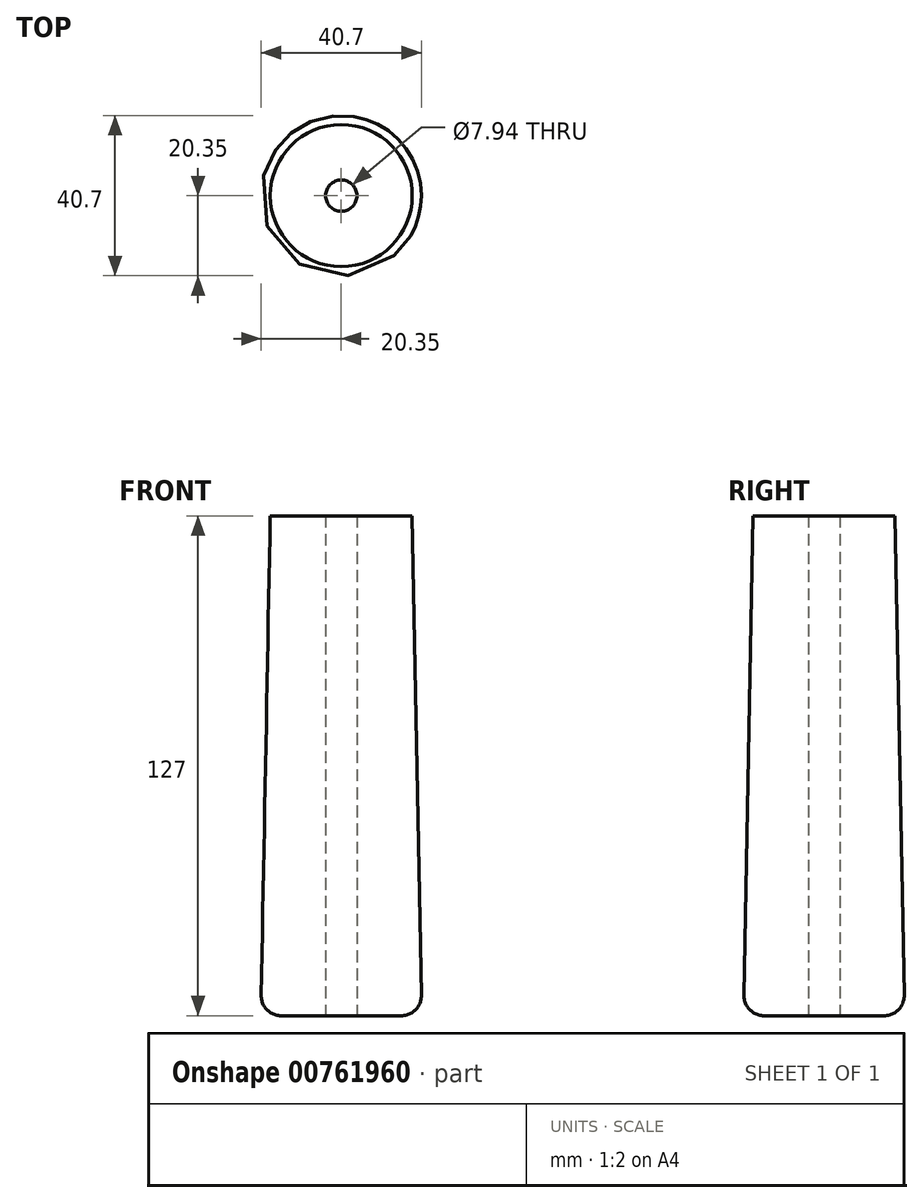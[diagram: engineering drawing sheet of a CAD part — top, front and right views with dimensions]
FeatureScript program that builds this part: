
annotation { "Feature Type Name" : "Feature", "Feature Type Description" : "" }
export const myFeature = defineFeature(function(context is Context, id is Id, definition is map)
    precondition{}
    {
        {
            var Q0;
            Q0=qCreatedBy(makeId("Top.planeOp"),FACE);
            var sketch = newSketch(context, id + "F0", { "sketchPlane" : qUnion([Q0])});
            skCircle(sketch, "E0", {"center": v(0, 0) * mm, "radius": 18.03 * mm});
            skSolve(sketch);
        }
        {
            var Q0;
            Q0=qCreatedBy(makeId("Top.planeOp"),FACE);
            cPlane(context, id + "F1", {"entities" : qUnion([Q0]), "cplaneType" : CPlaneType.OFFSET, "offset" : 127 * mm, "oppositeDirection" : true, "width" : 152.4 * mm, "height" : 152.4 * mm});
        }
        {
            var Q0;
            Q0=qCreatedBy(id+"F1.planeOp",FACE);
            var sketch = newSketch(context, id + "F2", { "sketchPlane" : qUnion([Q0])});
            skCircle(sketch, "E1", {"center": v(0, 0) * mm, "radius": 20.45 * mm});
            skSolve(sketch);
        }
        {
            var Q0;
            Q0=makeQuery(id+"F0.imprint","IMPRINT",FACE,{"disambiguationData":[TD([[makeQuery(id+"F0.imprint","IMPRINT",EDGE,{"derivedFrom":sQuery(id+"F0.wireOp",EDGE,"E0")}),1.0]])]});
            var Q1;
            Q1=makeQuery(id+"F2.imprint","IMPRINT",FACE,{"disambiguationData":[TD([[makeQuery(id+"F2.imprint","IMPRINT",EDGE,{"derivedFrom":sQuery(id+"F2.wireOp",EDGE,"E1")}),1.0]])]});
            loft(context, id + "F3", {"sheetProfilesArray" : [{ "sheetProfileEntities" : qUnion([Q0]) }, { "sheetProfileEntities" : qUnion([Q1]) }]});
        }
        {
            var Q0;
            Q0=makeQuery(id+"F3.opLoft","MID_CAP_EDGE",EDGE,{"disambiguationData":[OSD([sQuery(id+"F2.wireOp",EDGE,"E1")])],"capPos":1.0});
            fillet(context, id + "F4", {"entities" : qUnion([Q0]), "radius" : 5.08 * mm, "tangentPropagation" : true, "allowEdgeOverflow" : false});
        }
        {
            var Q0;
            Q0=makeQuery(id+"F3.opLoft","CAP_FACE",FACE,{"disambiguationData":[OSD([makeQuery(id+"F0.imprint","IMPRINT",FACE,{"disambiguationData":[TD([[makeQuery(id+"F0.imprint","IMPRINT",EDGE,{"derivedFrom":sQuery(id+"F0.wireOp",EDGE,"E0")}),1.0]])]})])],"isStart":true});
            var sketch = newSketch(context, id + "F5", { "sketchPlane" : qUnion([Q0])});
            skPoint(sketch, "E2", {"position": v(0, 0) * mm});
            skSolve(sketch);
        }
        {
            var Q0;
            Q0=sQuery(id+"F5.wireOp",VERTEX,"E2");
            var Q1;
            Q1=makeQuery(id+"F3.opLoft","SWEPT_BODY",BODY,{"disambiguationData":[OSD([makeQuery(id+"F0.imprint","IMPRINT",FACE,{"disambiguationData":[TD([[makeQuery(id+"F0.imprint","IMPRINT",EDGE,{"derivedFrom":sQuery(id+"F0.wireOp",EDGE,"E0")}),1.0]])]}),makeQuery(id+"F2.imprint","IMPRINT",FACE,{"disambiguationData":[TD([[makeQuery(id+"F2.imprint","IMPRINT",EDGE,{"derivedFrom":sQuery(id+"F2.wireOp",EDGE,"E1")}),1.0]])]})])]});
            hole(context, id + "F6", {"style" : HoleStyle.SIMPLE, "endStyle" : HoleEndStyle.THROUGH, "holeDiameter" : 7.94 * mm, "majorDiameter" : 6.35 * mm, "tappedDepth" : 12.7 * mm, "tapClearance" : 3, "locations" : qUnion([Q0]), "scope" : qUnion([Q1])});
        }
    });
